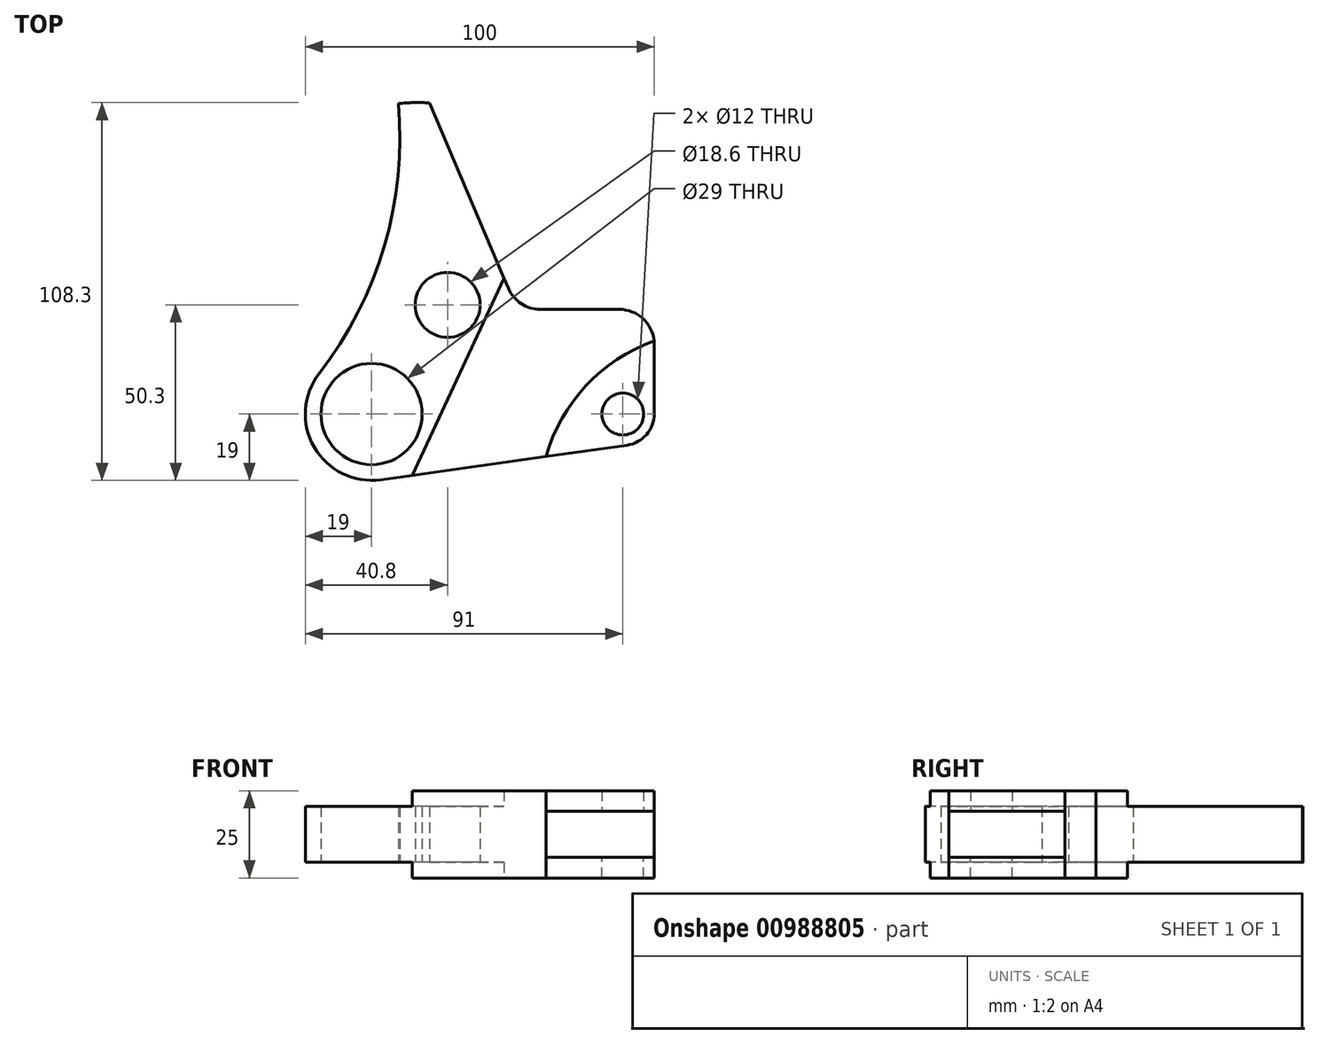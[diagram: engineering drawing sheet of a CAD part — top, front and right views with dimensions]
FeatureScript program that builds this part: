
annotation { "Feature Type Name" : "Feature", "Feature Type Description" : "" }
export const myFeature = defineFeature(function(context is Context, id is Id, definition is map)
    precondition{}
    {
        {
            var Q0;
            Q0=qCreatedBy(makeId("Top.planeOp"),FACE);
            var sketch = newSketch(context, id + "F0", { "sketchPlane" : qUnion([Q0])});
            skCircle(sketch, "E0", {"center": v(0, 0) * mm, "radius": 14.5 * mm});
            skCircle(sketch, "E1", {"center": v(72, 0) * mm, "radius": 6 * mm});
            skCircle(sketch, "E2", {"center": v(21.8, 31.3) * mm, "radius": 9.3 * mm});
            skArc(sketch, "E3", {"start": v(73.25, -8.91) * mm, "mid": v(78.8, -5.9) * mm, "end": v(81, 0) * mm});
            skLineSegment(sketch, "E4", {"start": v(81, 0) * mm, "end": v(81, 20) * mm});
            skLineSegment(sketch, "E5", {"start": v(2.64, -18.81) * mm, "end": v(73.25, -8.91) * mm});
            skArc(sketch, "E6", {"start": v(16.65, 89.17) * mm, "mid": v(12.15, 89.3) * mm, "end": v(7.65, 89.01) * mm});
            skLineSegment(sketch, "E7", {"start": v(71, 30) * mm, "end": v(48.39, 30) * mm});
            skLineSegment(sketch, "E8", {"start": v(16.65, 89.17) * mm, "end": v(39.18, 36.1) * mm});
            skArc(sketch, "E9.filletArc", {"start": v(81, 20) * mm, "mid": v(78.07, 27.07) * mm, "end": v(71, 30) * mm});
            skArc(sketch, "E10", {"start": v(-15, 11.65) * mm, "mid": v(3.67, 48.18) * mm, "end": v(7.65, 89.01) * mm});
            skPoint(sketch, "E11.visualSharp", {"position": v(41.77, 30) * mm});
            skArc(sketch, "E11.filletArc", {"start": v(39.18, 36.1) * mm, "mid": v(42.87, 31.66) * mm, "end": v(48.39, 30) * mm});
            skArc(sketch, "E12", {"start": v(-15, 11.65) * mm, "mid": v(-16.44, -9.52) * mm, "end": v(2.64, -18.81) * mm});
            skLineSegment(sketch, "E13", {"start": v(37.98, 38.92) * mm, "end": v(11.65, -17.55) * mm});
            skCircle(sketch, "E14", {"center": v(98, -26) * mm, "radius": 50 * mm});
            skSolve(sketch);
        }
        {
            var Q0;
            Q0=makeQuery(id+"F0.imprint","IMPRINT",FACE,{"disambiguationData":[TD([[makeQuery(id+"F0.imprint","IMPRINT",EDGE,{"derivedFrom":sQuery(id+"F0.wireOp",EDGE,"E0")}),-1.0]])]});
            extrude(context, id + "F1", {"entities" : qUnion([Q0]), "endBound" : BoundingType.SYMMETRIC, "depth" : 16 * mm, "offsetDistance" : 25 * mm});
        }
        {
            var Q0;
            {var subQ1=sQuery(id+"F0.wireOp",EDGE,"E7");Q0=makeQuery(id+"F0.imprint","IMPRINT",FACE,{"disambiguationData":[TD([[makeQuery(id+"F0.imprint","IMPRINT",EDGE,{"derivedFrom":subQ1}),1.0]])]});}
            extrude(context, id + "F2", {"entities" : qUnion([Q0]), "operationType" : NewBodyOperationType.ADD, "endBound" : BoundingType.SYMMETRIC, "depth" : 25 * mm, "offsetDistance" : 25 * mm});
        }
        {
            var Q0;
            Q0=makeQuery(id+"F0.imprint","IMPRINT",FACE,{"disambiguationData":[TD([[makeQuery(id+"F0.imprint","IMPRINT",EDGE,{"derivedFrom":sQuery(id+"F0.wireOp",EDGE,"E1")}),-1.0]])]});
            extrude(context, id + "F3", {"entities" : qUnion([Q0]), "endBound" : BoundingType.SYMMETRIC, "depth" : 13.2 * mm, "offsetDistance" : 25 * mm});
        }
        {
            var Q0;
            Q0=makeQuery(id+"F3.opExtrude","CAP_FACE",FACE,{"disambiguationData":[OSD([sQuery(id+"F0.wireOp",EDGE,"E1"),sQuery(id+"F0.wireOp",EDGE,"E3"),sQuery(id+"F0.wireOp",EDGE,"E4"),sQuery(id+"F0.wireOp",EDGE,"E5"),sQuery(id+"F0.wireOp",EDGE,"E9.filletArc"),sQuery(id+"F0.wireOp",EDGE,"E14")])],"isStart":false});
            var Q1;
            Q1=makeQuery(id+"F2.opExtrude","CAP_FACE",FACE,{"disambiguationData":[OSD([sQuery(id+"F0.wireOp",EDGE,"E5"),sQuery(id+"F0.wireOp",EDGE,"E7"),sQuery(id+"F0.wireOp",EDGE,"E8"),sQuery(id+"F0.wireOp",EDGE,"E9.filletArc"),sQuery(id+"F0.wireOp",EDGE,"E11.filletArc"),sQuery(id+"F0.wireOp",EDGE,"E13"),sQuery(id+"F0.wireOp",EDGE,"E14")])],"isStart":false});
            extrude(context, id + "F4", {"entities" : qUnion([Q0]), "endBound" : BoundingType.UP_TO_SURFACE, "depth" : 25 * mm, "endBoundEntityFace" : qUnion([Q1]), "offsetDistance" : 25 * mm});
        }
        {
            var Q0;
            Q0=makeQuery(id+"F3.opExtrude","CAP_FACE",FACE,{"disambiguationData":[OSD([sQuery(id+"F0.wireOp",EDGE,"E1"),sQuery(id+"F0.wireOp",EDGE,"E3"),sQuery(id+"F0.wireOp",EDGE,"E4"),sQuery(id+"F0.wireOp",EDGE,"E5"),sQuery(id+"F0.wireOp",EDGE,"E9.filletArc"),sQuery(id+"F0.wireOp",EDGE,"E14")])],"isStart":true});
            var Q1;
            Q1=makeQuery(id+"F2.opExtrude","CAP_FACE",FACE,{"disambiguationData":[OSD([sQuery(id+"F0.wireOp",EDGE,"E5"),sQuery(id+"F0.wireOp",EDGE,"E7"),sQuery(id+"F0.wireOp",EDGE,"E8"),sQuery(id+"F0.wireOp",EDGE,"E9.filletArc"),sQuery(id+"F0.wireOp",EDGE,"E11.filletArc"),sQuery(id+"F0.wireOp",EDGE,"E13"),sQuery(id+"F0.wireOp",EDGE,"E14")])],"isStart":true});
            extrude(context, id + "F5", {"entities" : qUnion([Q0]), "endBound" : BoundingType.UP_TO_SURFACE, "depth" : 25 * mm, "endBoundEntityFace" : qUnion([Q1]), "offsetDistance" : 25 * mm});
        }
        {
            var Q0;
            Q0=makeQuery(id+"F3.opExtrude","SWEPT_BODY",BODY,{"disambiguationData":[OSD([sQuery(id+"F0.wireOp",EDGE,"E1"),sQuery(id+"F0.wireOp",EDGE,"E3"),sQuery(id+"F0.wireOp",EDGE,"E4"),sQuery(id+"F0.wireOp",EDGE,"E5"),sQuery(id+"F0.wireOp",EDGE,"E9.filletArc"),sQuery(id+"F0.wireOp",EDGE,"E14")])]});
            var Q1;
            Q1=makeQuery(id+"F4.opExtrude","SWEPT_BODY",BODY,{"disambiguationData":[OSD([sQuery(id+"F0.wireOp",EDGE,"E1"),sQuery(id+"F0.wireOp",EDGE,"E3"),sQuery(id+"F0.wireOp",EDGE,"E4"),sQuery(id+"F0.wireOp",EDGE,"E5"),sQuery(id+"F0.wireOp",EDGE,"E9.filletArc"),sQuery(id+"F0.wireOp",EDGE,"E14")])]});
            booleanBodies(context, id + "F6", {"operationType" : BooleanOperationType.SUBTRACTION, "tools" : qUnion([Q0]), "targets" : qUnion([Q1])});
        }
    });
